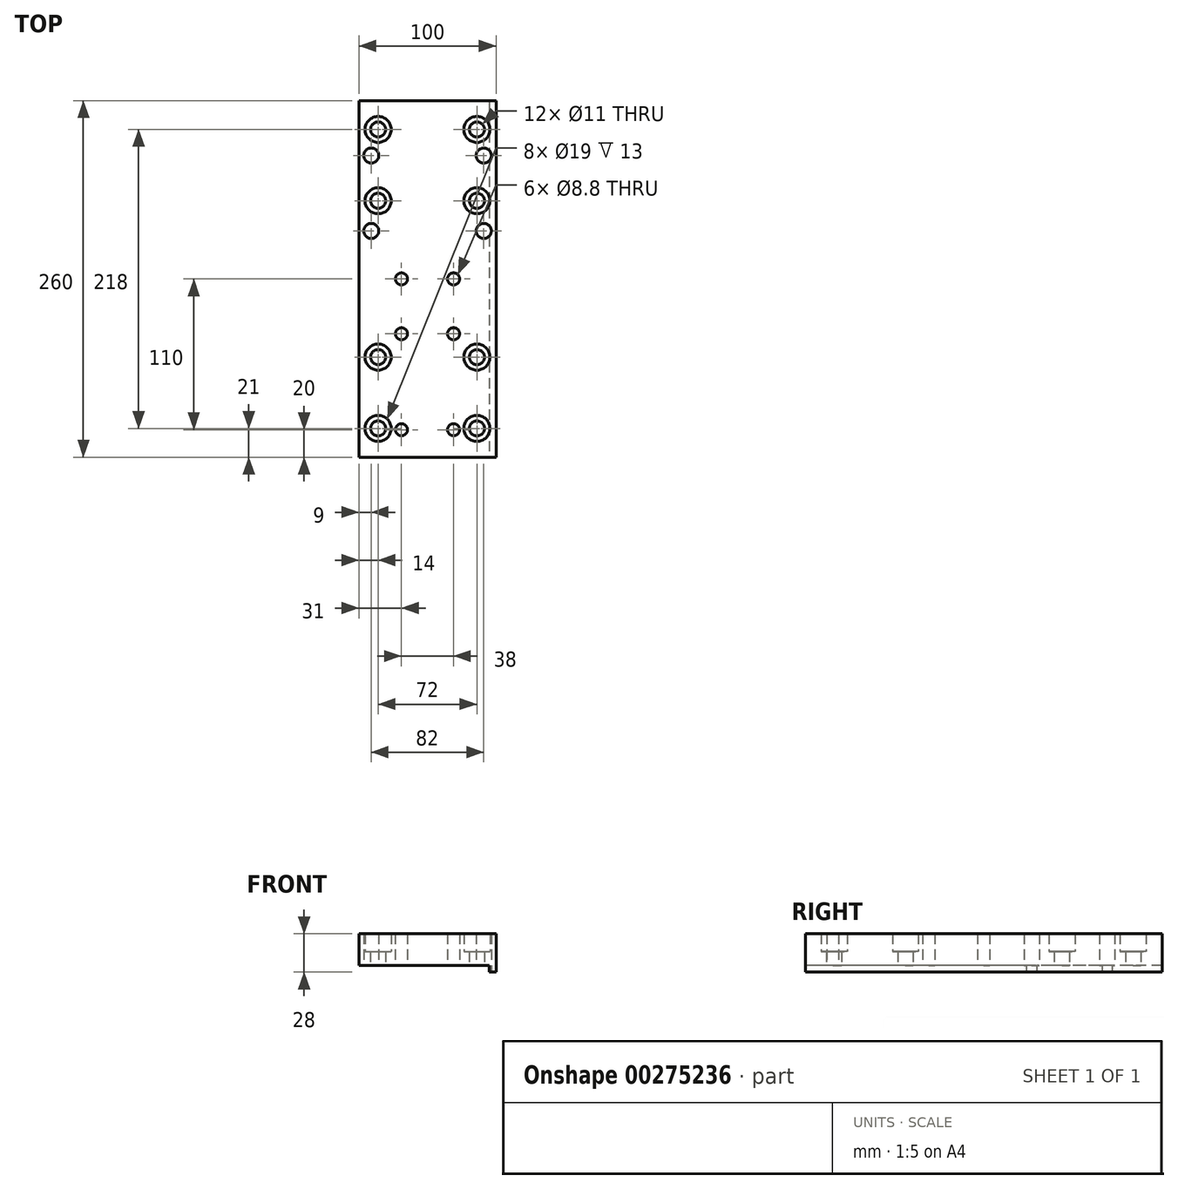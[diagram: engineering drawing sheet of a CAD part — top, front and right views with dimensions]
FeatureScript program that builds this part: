
annotation { "Feature Type Name" : "Feature", "Feature Type Description" : "" }
export const myFeature = defineFeature(function(context is Context, id is Id, definition is map)
    precondition{}
    {
        {
            var Q0;
            Q0=qCreatedBy(makeId("Front.planeOp"),FACE);
            var sketch = newSketch(context, id + "F0", { "sketchPlane" : qUnion([Q0])});
            skLineSegment(sketch, "E0", {"start": v(0, 23) * mm, "end": v(100, 23) * mm});
            skLineSegment(sketch, "E1", {"start": v(100, 23) * mm, "end": v(100, -5) * mm});
            skLineSegment(sketch, "E2", {"start": v(100, -5) * mm, "end": v(95, -5) * mm});
            skLineSegment(sketch, "E3", {"start": v(95, -5) * mm, "end": v(95, 0) * mm});
            skLineSegment(sketch, "E4", {"start": v(95, 0) * mm, "end": v(0, 0) * mm});
            skLineSegment(sketch, "E5", {"start": v(0, 0) * mm, "end": v(0, 23) * mm});
            skSolve(sketch);
        }
        {
            var Q0;
            Q0 = qSketchRegion(id + "F0", true);
            extrude(context, id + "F1", {"entities" : qUnion([Q0]), "oppositeDirection" : true, "depth" : 260 * mm});
        }
        {
            var Q0;
            Q0=makeQuery(id+"F1.opExtrude","SWEPT_FACE",FACE,{"disambiguationData":[OSD([sQuery(id+"F0.wireOp",EDGE,"E0")])]});
            var sketch = newSketch(context, id + "F2", { "sketchPlane" : qUnion([Q0])});
            skLineSegment(sketch, "E6", {"start": v(50, 260) * mm, "end": v(50, 329.16) * mm, "construction": true});
            skLineSegment(sketch, "E7", {"start": v(50, 329.16) * mm, "end": v(50, -121.28) * mm, "construction": true});
            skLineSegment(sketch, "E8", {"start": v(14, 329.16) * mm, "end": v(14, -122.56) * mm, "construction": true});
            skLineSegment(sketch, "E9", {"start": v(86, 329.16) * mm, "end": v(86, -121.1) * mm, "construction": true});
            skCircle(sketch, "E10", {"center": v(14, 239) * mm, "radius": 7.28 * mm});
            skCircle(sketch, "E11", {"center": v(14, 187) * mm, "radius": 8.04 * mm});
            skCircle(sketch, "E12", {"center": v(86, 239) * mm, "radius": 10.05 * mm});
            skCircle(sketch, "E13", {"center": v(86, 187) * mm, "radius": 8.61 * mm});
            skLineSegment(sketch, "E14", {"start": v(-107.4, 130) * mm, "end": v(213.85, 130) * mm, "construction": true});
            skPoint(sketch, "E14.startSnap0", {"position": v(0, 130) * mm});
            skCircle(sketch, "E15.MirrorC", {"center": v(86, 73) * mm, "radius": 8.61 * mm});
            skCircle(sketch, "E16.MirrorC", {"center": v(86, 21) * mm, "radius": 10.05 * mm});
            skCircle(sketch, "E17.MirrorC", {"center": v(14, 21) * mm, "radius": 7.28 * mm});
            skCircle(sketch, "E18.MirrorC", {"center": v(14, 73) * mm, "radius": 8.04 * mm});
            skLineSegment(sketch, "E19", {"start": v(9, 314.8) * mm, "end": v(9, -24.81) * mm, "construction": true});
            skLineSegment(sketch, "E20", {"start": v(91, 314.8) * mm, "end": v(91, -50.97) * mm, "construction": true});
            skCircle(sketch, "E21", {"center": v(91, 220) * mm, "radius": 3.95 * mm});
            skCircle(sketch, "E22", {"center": v(9, 220) * mm, "radius": 3.62 * mm});
            skCircle(sketch, "E23", {"center": v(91, 165) * mm, "radius": 4.16 * mm});
            skCircle(sketch, "E24", {"center": v(9, 165) * mm, "radius": 3.2 * mm});
            skLineSegment(sketch, "E25", {"start": v(31, 173.5) * mm, "end": v(31, -23.79) * mm, "construction": true});
            skLineSegment(sketch, "E26", {"start": v(69, 173.5) * mm, "end": v(69, -29.16) * mm, "construction": true});
            skCircle(sketch, "E27", {"center": v(31, 20) * mm, "radius": 6.28 * mm});
            skCircle(sketch, "E28", {"center": v(69, 20) * mm, "radius": 4.68 * mm});
            skCircle(sketch, "E29", {"center": v(31, 90) * mm, "radius": 5.44 * mm});
            skCircle(sketch, "E30", {"center": v(69, 90) * mm, "radius": 6.1 * mm});
            skCircle(sketch, "E31", {"center": v(31, 130) * mm, "radius": 7.62 * mm});
            skCircle(sketch, "E32", {"center": v(69, 130) * mm, "radius": 6.73 * mm});
            skSolve(sketch);
        }
        {
            var Q0;
            Q0=sQuery(id+"F2.wireOp",VERTEX,"E10.center");
            var Q1;
            Q1=sQuery(id+"F2.wireOp",VERTEX,"E12.center");
            var Q2;
            Q2=sQuery(id+"F2.wireOp",VERTEX,"E11.center");
            var Q3;
            Q3=sQuery(id+"F2.wireOp",VERTEX,"E13.center");
            var Q4;
            Q4=sQuery(id+"F2.wireOp",VERTEX,"E15.MirrorC.center");
            var Q5;
            Q5=sQuery(id+"F2.wireOp",VERTEX,"E16.MirrorC.center");
            var Q6;
            Q6=sQuery(id+"F2.wireOp",VERTEX,"E18.MirrorC.center");
            var Q7;
            Q7=sQuery(id+"F2.wireOp",VERTEX,"E17.MirrorC.center");
            var Q8;
            Q8=makeQuery(id+"F1.opExtrude","SWEPT_BODY",BODY,{"disambiguationData":[OSD([sQuery(id+"F0.wireOp",EDGE,"E0"),sQuery(id+"F0.wireOp",EDGE,"E1"),sQuery(id+"F0.wireOp",EDGE,"E2"),sQuery(id+"F0.wireOp",EDGE,"E3"),sQuery(id+"F0.wireOp",EDGE,"E4"),sQuery(id+"F0.wireOp",EDGE,"E5")])]});
            hole(context, id + "F3", {"style" : HoleStyle.C_BORE, "endStyle" : HoleEndStyle.BLIND, "holeDiameter" : 11 * mm, "cBoreDiameter" : 19 * mm, "cBoreDepth" : 13 * mm, "holeDepth" : 30 * mm, "tappedDepth" : 12 * mm, "tapClearance" : 3, "startFromSketch" : true, "locations" : qUnion([Q0, Q1, Q2, Q3, Q4, Q5, Q6, Q7]), "scope" : qUnion([Q8])});
        }
        {
            var Q0;
            Q0=sQuery(id+"F2.wireOp",VERTEX,"E27.center");
            var Q1;
            Q1=sQuery(id+"F2.wireOp",VERTEX,"E28.center");
            var Q2;
            Q2=sQuery(id+"F2.wireOp",VERTEX,"E29.center");
            var Q3;
            Q3=sQuery(id+"F2.wireOp",VERTEX,"E30.center");
            var Q4;
            Q4=sQuery(id+"F2.wireOp",VERTEX,"E31.center");
            var Q5;
            Q5=sQuery(id+"F2.wireOp",VERTEX,"E32.center");
            var Q6;
            Q6=makeQuery(id+"F1.opExtrude","SWEPT_BODY",BODY,{"disambiguationData":[OSD([sQuery(id+"F0.wireOp",EDGE,"E0"),sQuery(id+"F0.wireOp",EDGE,"E1"),sQuery(id+"F0.wireOp",EDGE,"E2"),sQuery(id+"F0.wireOp",EDGE,"E3"),sQuery(id+"F0.wireOp",EDGE,"E4"),sQuery(id+"F0.wireOp",EDGE,"E5")])]});
            hole(context, id + "F4", {"style" : HoleStyle.SIMPLE, "endStyle" : HoleEndStyle.BLIND, "standardTappedOrClearance" : lookupTablePath({ "standard" : "ISO", "fit" : "Normal", "size" : "M8", "type" : "Clearance" }), "standardBlindInLast" : lookupTablePath({ "fit" : "Standard", "standard" : "ISO", "size" : "M8", "type" : "Clearance" }), "holeDiameter" : 8.8 * mm, "holeDepth" : 30 * mm, "tappedDepth" : 12 * mm, "tapClearance" : 3, "startFromSketch" : true, "locations" : qUnion([Q0, Q1, Q2, Q3, Q4, Q5]), "scope" : qUnion([Q6])});
        }
        {
            var Q0;
            Q0=sQuery(id+"F2.wireOp",VERTEX,"E22.center");
            var Q1;
            Q1=sQuery(id+"F2.wireOp",VERTEX,"E21.center");
            var Q2;
            Q2=sQuery(id+"F2.wireOp",VERTEX,"E23.center");
            var Q3;
            Q3=sQuery(id+"F2.wireOp",VERTEX,"E24.center");
            var Q4;
            Q4=makeQuery(id+"F1.opExtrude","SWEPT_BODY",BODY,{"disambiguationData":[OSD([sQuery(id+"F0.wireOp",EDGE,"E0"),sQuery(id+"F0.wireOp",EDGE,"E1"),sQuery(id+"F0.wireOp",EDGE,"E2"),sQuery(id+"F0.wireOp",EDGE,"E3"),sQuery(id+"F0.wireOp",EDGE,"E4"),sQuery(id+"F0.wireOp",EDGE,"E5")])]});
            hole(context, id + "F5", {"style" : HoleStyle.SIMPLE, "endStyle" : HoleEndStyle.BLIND, "standardTappedOrClearance" : lookupTablePath({ "standard" : "ISO", "fit" : "Normal", "size" : "M10", "type" : "Clearance" }), "standardBlindInLast" : lookupTablePath({ "fit" : "Standard", "standard" : "ISO", "size" : "M10", "type" : "Clearance" }), "holeDiameter" : 11 * mm, "holeDepth" : 30 * mm, "tappedDepth" : 12 * mm, "tapClearance" : 3, "startFromSketch" : true, "locations" : qUnion([Q0, Q1, Q2, Q3]), "scope" : qUnion([Q4])});
        }
    });
